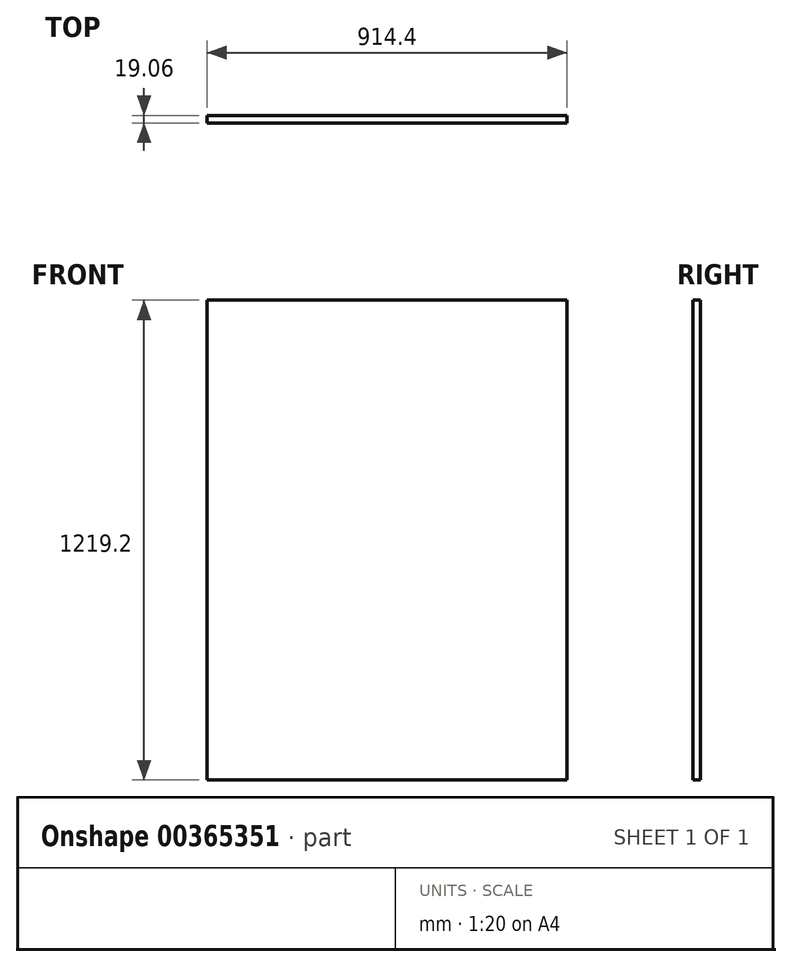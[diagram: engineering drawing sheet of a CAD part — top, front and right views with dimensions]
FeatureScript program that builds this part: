
annotation { "Feature Type Name" : "Feature", "Feature Type Description" : "" }
export const myFeature = defineFeature(function(context is Context, id is Id, definition is map)
    precondition{}
    {
        {
            var Q0;
            Q0=qCreatedBy(makeId("Front.planeOp"),FACE);
            var sketch = newSketch(context, id + "F0", { "sketchPlane" : qUnion([Q0])});
            skLineSegment(sketch, "E0.bottom", {"start": v(-457.2, 609.6) * mm, "end": v(457.2, 609.6) * mm});
            skLineSegment(sketch, "E0.top", {"start": v(-457.2, -609.6) * mm, "end": v(457.2, -609.6) * mm});
            skLineSegment(sketch, "E0.left", {"start": v(-457.2, 609.6) * mm, "end": v(-457.2, -609.6) * mm});
            skLineSegment(sketch, "E0.right", {"start": v(457.2, 609.6) * mm, "end": v(457.2, -609.6) * mm});
            skPoint(sketch, "E0.middle", {"position": v(0, 0) * mm});
            skSolve(sketch);
        }
        {
            var Q0;
            Q0=makeQuery(id+"F0.imprint","IMPRINT",FACE,{"disambiguationData":[TD([[makeQuery(id+"F0.imprint","IMPRINT",EDGE,{"derivedFrom":sQuery(id+"F0.wireOp",EDGE,"E0.bottom")}),-1.0]])]});
            extrude(context, id + "F1", {"entities" : qUnion([Q0]), "endBound" : BoundingType.SYMMETRIC, "depth" : 19.05 * mm, "offsetDistance" : 25.4 * mm});
        }
    });
